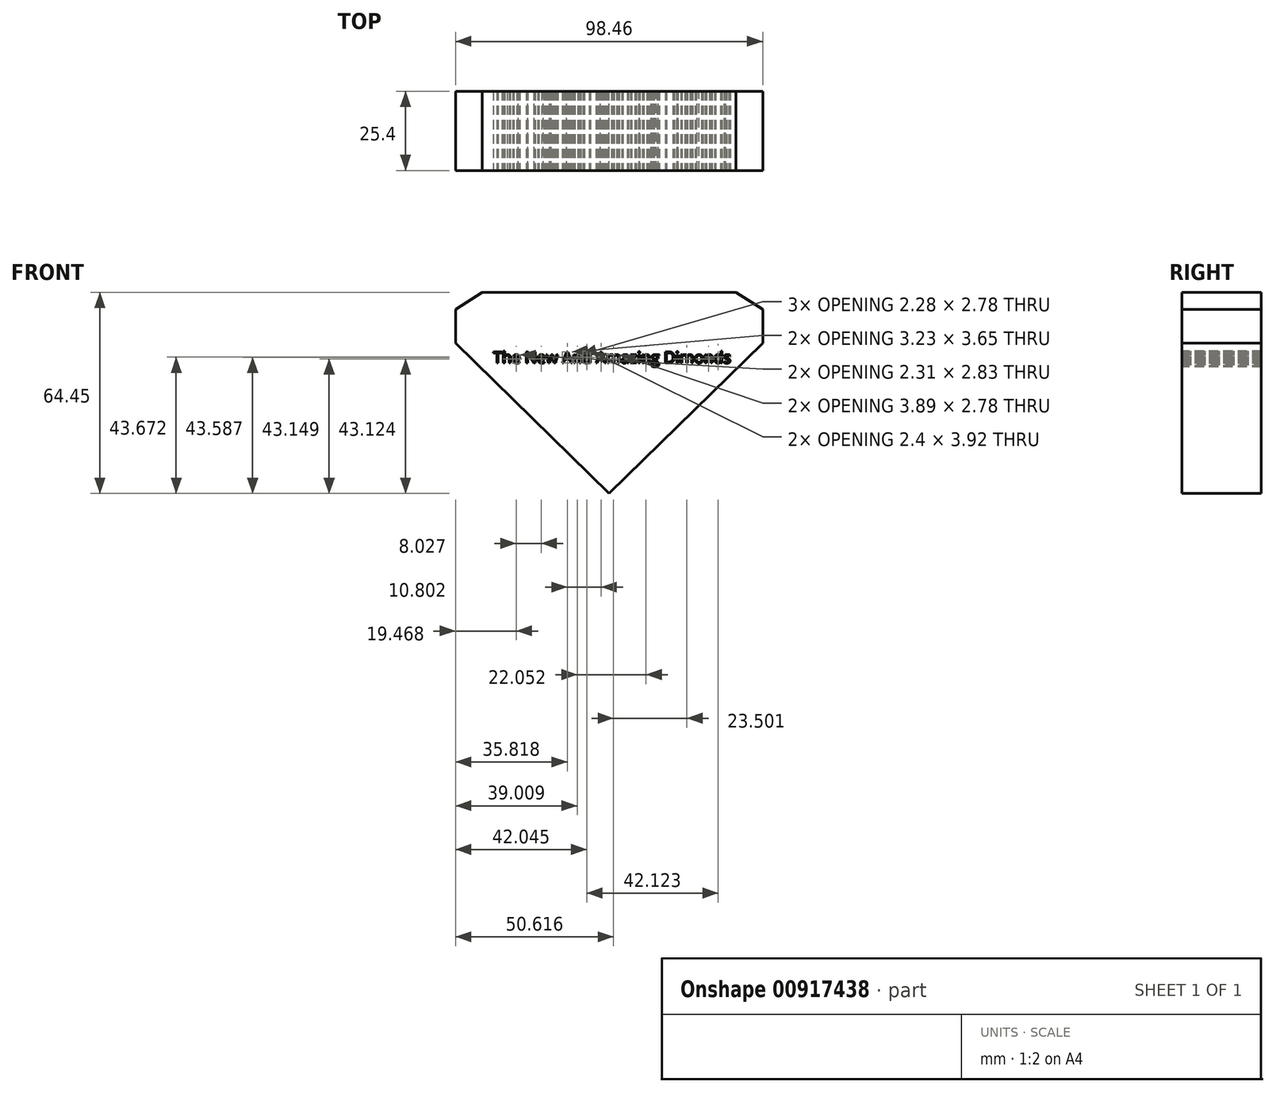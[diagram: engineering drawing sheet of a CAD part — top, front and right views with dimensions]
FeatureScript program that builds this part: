
annotation { "Feature Type Name" : "Feature", "Feature Type Description" : "" }
export const myFeature = defineFeature(function(context is Context, id is Id, definition is map)
    precondition{}
    {
        {
            var Q0;
            Q0=qCreatedBy(makeId("Front.planeOp"),FACE);
            var sketch = newSketch(context, id + "F0", { "sketchPlane" : qUnion([Q0])});
            skLineSegment(sketch, "E0", {"start": v(-49.23, 19.18) * mm, "end": v(0, -28.93) * mm});
            skLineSegment(sketch, "E1", {"start": v(-49.23, 19.18) * mm, "end": v(-49.23, 29.99) * mm});
            skLineSegment(sketch, "E2", {"start": v(-49.23, 29.99) * mm, "end": v(-40.66, 35.52) * mm});
            skLineSegment(sketch, "E3", {"start": v(-40.66, 35.52) * mm, "end": v(0, 35.52) * mm});
            skLineSegment(sketch, "E4.MirrorCS", {"start": v(40.66, 35.52) * mm, "end": v(0, 35.52) * mm});
            skLineSegment(sketch, "E5.MirrorCS", {"start": v(49.23, 29.99) * mm, "end": v(40.66, 35.52) * mm});
            skLineSegment(sketch, "E6.MirrorCS", {"start": v(49.23, 19.18) * mm, "end": v(49.23, 29.99) * mm});
            skLineSegment(sketch, "E7.MirrorCS", {"start": v(49.23, 19.18) * mm, "end": v(0, -28.93) * mm});
            skSolve(sketch);
        }
        {
            var Q0;
            Q0=makeQuery(id+"F0.imprint","IMPRINT",FACE,{"disambiguationData":[TD([[makeQuery(id+"F0.imprint","IMPRINT",EDGE,{"derivedFrom":sQuery(id+"F0.wireOp",EDGE,"E0")}),1.0]])]});
            extrude(context, id + "F1", {"entities" : qUnion([Q0]), "depth" : 25.4 * mm, "offsetDistance" : 25.4 * mm});
        }
        {
            var Q0;
            Q0=makeQuery(id+"F1.opExtrude","CAP_FACE",FACE,{"disambiguationData":[OSD([sQuery(id+"F0.wireOp",EDGE,"E0"),sQuery(id+"F0.wireOp",EDGE,"E1"),sQuery(id+"F0.wireOp",EDGE,"E2"),sQuery(id+"F0.wireOp",EDGE,"E3"),sQuery(id+"F0.wireOp",EDGE,"E4.MirrorCS"),sQuery(id+"F0.wireOp",EDGE,"E5.MirrorCS"),sQuery(id+"F0.wireOp",EDGE,"E6.MirrorCS"),sQuery(id+"F0.wireOp",EDGE,"E7.MirrorCS")])],"isStart":false});
            var sketch = newSketch(context, id + "F2", { "sketchPlane" : qUnion([Q0])});
            skText(sketch, "E8", { "text": "The New And Amazing Dimonds", "fontName": "OpenSans-Regular.ttf"});
            const initialGuessF2  = {"E8": [-0.03715, 0.01283, 1, 0, 0.00367]};
            skSetInitialGuess(sketch, initialGuessF2);
            skSolve(sketch);
        }
        {
            var Q0;
            Q0 = qSketchRegion(id + "F2", true);
            extrude(context, id + "F3", {"entities" : qUnion([Q0]), "operationType" : NewBodyOperationType.REMOVE, "oppositeDirection" : true, "depth" : 25.4 * mm, "offsetDistance" : 25.4 * mm});
        }
    });
